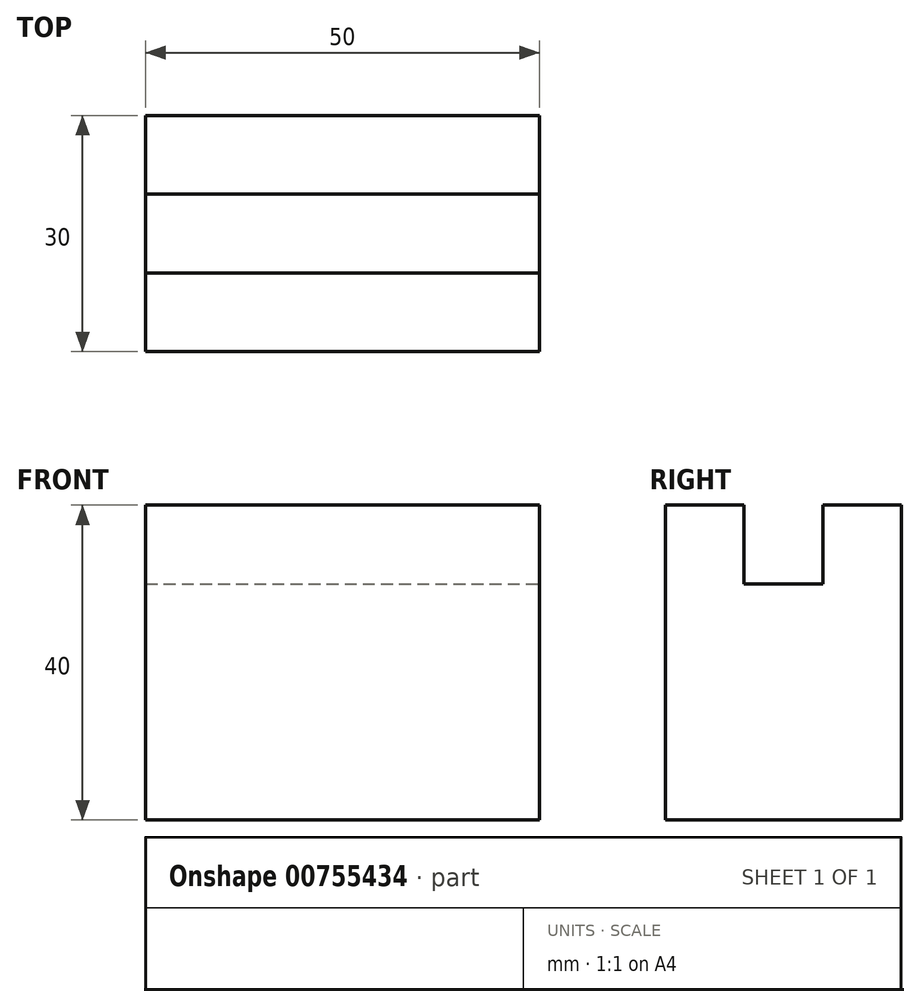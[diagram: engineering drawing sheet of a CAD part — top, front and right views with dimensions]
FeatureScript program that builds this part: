
annotation { "Feature Type Name" : "Feature", "Feature Type Description" : "" }
export const myFeature = defineFeature(function(context is Context, id is Id, definition is map)
    precondition{}
    {
        {
            var Q0;
            Q0=qCreatedBy(makeId("Front.planeOp"),FACE);
            var sketch = newSketch(context, id + "F0", { "sketchPlane" : qUnion([Q0])});
            skLineSegment(sketch, "E0", {"start": v(0, 0) * mm, "end": v(50, 0) * mm});
            skLineSegment(sketch, "E1", {"start": v(50, 0) * mm, "end": v(50, 40) * mm});
            skLineSegment(sketch, "E2", {"start": v(50, 40) * mm, "end": v(0, 40) * mm});
            skLineSegment(sketch, "E3", {"start": v(0, 40) * mm, "end": v(0, 0) * mm});
            skSolve(sketch);
        }
        {
            var Q0;
            Q0=makeQuery(id+"F0.imprint","IMPRINT",FACE,{"disambiguationData":[TD([[makeQuery(id+"F0.imprint","IMPRINT",EDGE,{"derivedFrom":sQuery(id+"F0.wireOp",EDGE,"E0")}),1.0]])]});
            extrude(context, id + "F1", {"entities" : qUnion([Q0]), "depth" : 30 * mm, "offsetDistance" : 25 * mm});
        }
        {
            var Q0;
            Q0=makeQuery(id+"F1.opExtrude","SWEPT_FACE",FACE,{"disambiguationData":[OSD([sQuery(id+"F0.wireOp",EDGE,"E1")])]});
            var sketch = newSketch(context, id + "F2", { "sketchPlane" : qUnion([Q0])});
            skLineSegment(sketch, "E4", {"start": v(0, 40) * mm, "end": v(-10, 40) * mm});
            skLineSegment(sketch, "E5", {"start": v(-10, 40) * mm, "end": v(-10, 30) * mm});
            skLineSegment(sketch, "E6", {"start": v(-10, 30) * mm, "end": v(-20, 30) * mm});
            skLineSegment(sketch, "E7", {"start": v(-20, 30) * mm, "end": v(-20, 40) * mm});
            skLineSegment(sketch, "E8", {"start": v(-20, 40) * mm, "end": v(-30, 40) * mm});
            skLineSegment(sketch, "E9", {"start": v(-30, 40) * mm, "end": v(-10, 40) * mm});
            skSolve(sketch);
        }
        {
            var Q0;
            {var subQ0=sQuery(id+"F2.wireOp",EDGE,"E5");Q0=makeQuery(id+"F2.imprint","IMPRINT",FACE,{"disambiguationData":[TD([[makeQuery(id+"F2.imprint","IMPRINT",EDGE,{"derivedFrom":subQ0}),-1.0]])]});}
            extrude(context, id + "F3", {"entities" : qUnion([Q0]), "operationType" : NewBodyOperationType.ADD, "depth" : 50 * mm, "offsetDistance" : 25 * mm});
        }
        {
            var Q0;
            Q0=makeQuery(id+"F3.opExtrude","CAP_FACE",FACE,{"disambiguationData":[OSD([sQuery(id+"F2.wireOp",EDGE,"E5"),sQuery(id+"F2.wireOp",EDGE,"E6"),sQuery(id+"F2.wireOp",EDGE,"E7"),sQuery(id+"F2.wireOp",EDGE,"E9")])],"isStart":false});
            extrude(context, id + "F4", {"entities" : qUnion([Q0]), "operationType" : NewBodyOperationType.REMOVE, "oppositeDirection" : true, "depth" : 100 * mm, "offsetDistance" : 25 * mm});
        }
    });
